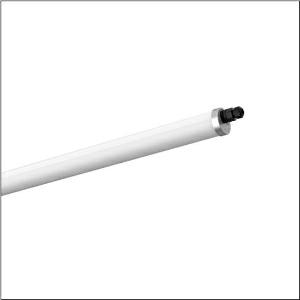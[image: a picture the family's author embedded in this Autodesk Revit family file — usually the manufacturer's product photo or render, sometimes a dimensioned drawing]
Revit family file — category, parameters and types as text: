
# Revit family: monsun_r__31_tube_51ft107n460a_2b58
name_source: partatom
category: Lighting Fixtures
units: mm (PartAtom-declared; Revit-internal decimal feet)

## family parameters
Cut with Voids When Loaded = No
Host = Face
Light Source = No
Part Type = Normal
Room Calculation Point = No
Round Connector Dimension = Use Diameter
Shared = No

## types (1)
- Monsun® 31 Tube (1 x LED, 6500 lm, 40 W, 4000K)
    Apparent Load = 40 VA
    CIE Flux Codes = 42 71 90 91 100
    Color Rendering = 80
    Color Temperature = 4000K
    Default Elevation = 1800 mm
    Description = Monsun® 31 Tube, tubular luminaire, primary optical cover: diffuser, of PMMA, light emission: direct distribution, primary light characteristic: symmetric, installation type: suspended mounting, surface-mounted, LED, rated luminous flux: 6.500lm, luminous efficacy: 160lm/W, light colour: 840, colour temperature: 4000K, with with 1 terminal, 3-pole, max. 2.5mm², through-wiring: 3x 1.5mm², mains connection: 220..240V, AC, 50/60Hz, rated input power: 40W, housing, cylindrical, of PMMA, semi-transparent, matt white, with luminaire and ceiling fastening, V4A, mounting with brackets of stainless steel, length: 1.560mm, diameter: 75mm, end cap, of stainless steel (V4A), protection rating (complete): IP67/IP69K, insulation class (complete): insulation class I (protective earthing), certification: CE, UKCA, impact resistance: IK07, permissible operating ambient temperature: -20..+40°C, corresponds to IFS (International Featured Standards) requirements for safety and quality in the food industry, usage in unprotected outdoor area possible with horizontal mounting, contact your sales advisor before using the luminaires in applications with unclear chemical exposure, large temperature fluctuations or condensation-forming humidity, packaging unit: 1 piece
    Height = 83 mm
    Lamp = 1 x LED
    Lamp Light Flux = 6500 lm
    Lamp Power = 40 W
    Lamp count = 1
    Length = 1560 mm
    Luminous efficacy = 163 lm/W
    Manufacturer = Siteco
    ModVariant = No
    Model = 51FT107N460A
    Mounting Place = Ceiling
    Mounting Type = Pendant
    Number of Poles = 1
    OnlyDefault = Yes
    Power Factor = 1
    Product Name = Monsun® 31 Tube
    Product group = tubular luminaire
    ProductGroupID = 906
    Protection Class = Protection class I
    RLX_Detail_Level = 1
    RLX_Emergency_Light_Flux = 0 lm
    RLX_Emergency_Type = 0
    RLX_Emergency_Type_DB = No
    RlxData = <blob elided: 25233 chars, md5=c8cfa2e6>
    Socket = socket
    Standby Power = 0 W
    System Light Flux = 6500 lm
    System Power = 40 W
    Type Comments = Product without accessories
    Type Image = l_1228461.jpg
    URL = http://relux.com
    VarID = ---
    Voltage = 0 V
    Weight = 0.00 kg
    Width = 75 mm

## geometry (parser evidence)
native form markers: Blend x4, Sweep x14
no freeform markers — native parametric forms only
